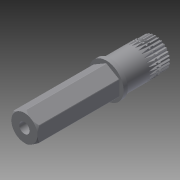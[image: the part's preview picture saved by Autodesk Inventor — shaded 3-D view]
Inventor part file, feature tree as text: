
AUTODESK INVENTOR PART (.ipt)
format: ipt  version: 2014 (Build 180170000, 170)  size: 2,081,280 bytes
history: native  units: in
note: dims shown in document units (in); Inventor stores cm internally (conversion verified against a paired STEP export)
features: fillet x1, imported_body x1
ambient origin geometry x8: Origin, YZ Plane, XZ Plane, XY Plane, X Axis, Y Axis, Z Axis, Center Point
bodies: Body1 (feature_tree)
feature tree (2):
  fillet  "Fillet5"  [1 undecoded]
  imported_body  "Base1"
note: 1 required parameter value undecoded (feature->parameter linkage not recoverable at this tier; creation-order binding heuristic only, values carry confidence <= 0.55)
